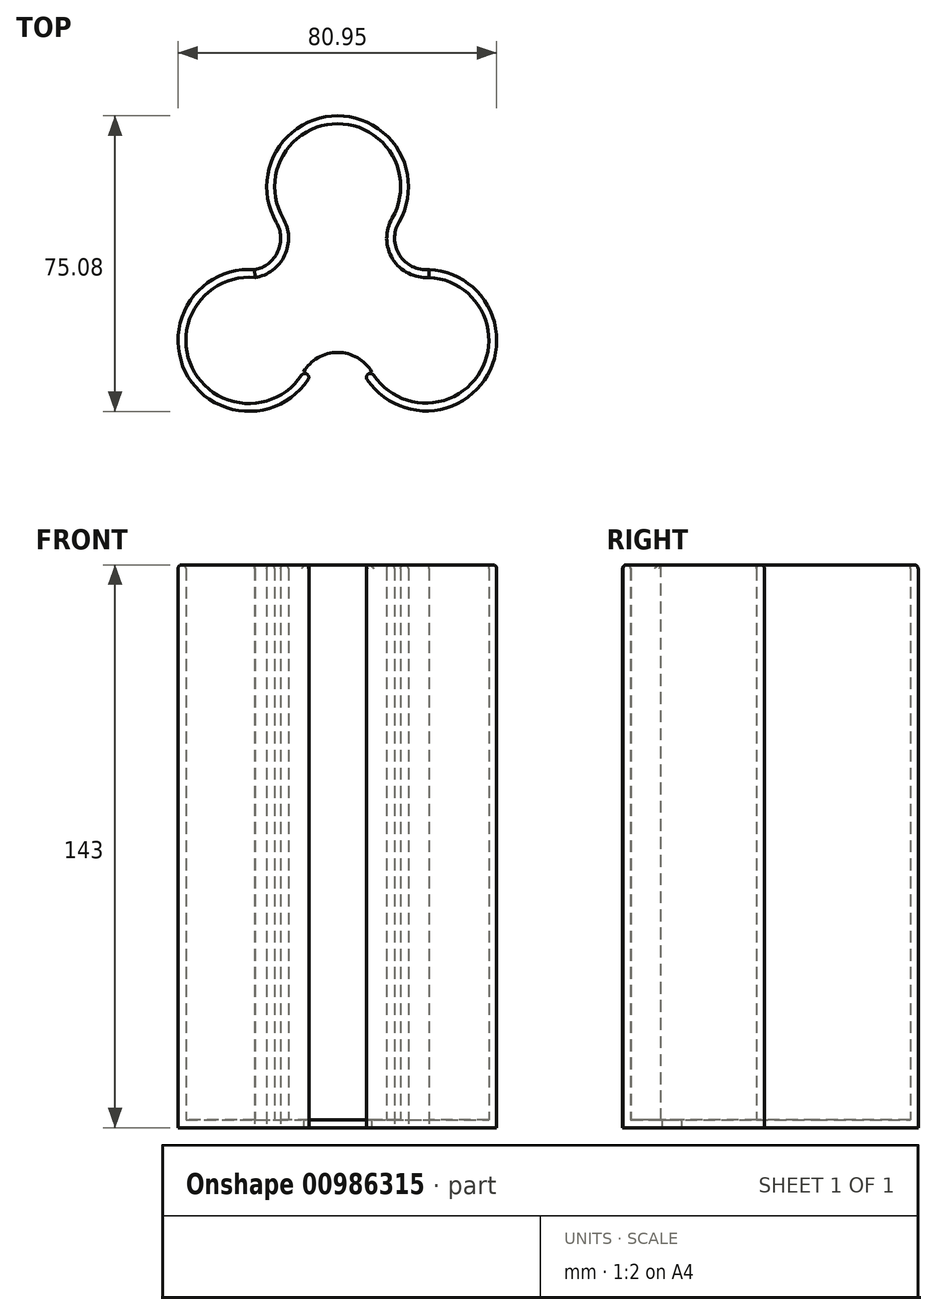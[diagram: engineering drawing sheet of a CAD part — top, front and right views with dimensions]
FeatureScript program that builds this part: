
annotation { "Feature Type Name" : "Feature", "Feature Type Description" : "" }
export const myFeature = defineFeature(function(context is Context, id is Id, definition is map)
    precondition{}
    {
        {
            var Q0;
            Q0=qCreatedBy(makeId("Top.planeOp"),FACE);
            var sketch = newSketch(context, id + "F0", { "sketchPlane" : qUnion([Q0])});
            skArc(sketch, "E0", {"start": v(13, 18.5) * mm, "mid": v(0, 41) * mm, "end": v(-13, 18.5) * mm});
            skArc(sketch, "E1.1.0", {"start": v(-24.16, 1.87) * mm, "mid": v(-35.1, -21.26) * mm, "end": v(-9.53, -20.6) * mm});
            skArc(sketch, "E1.2.0", {"start": v(15.06, 0.04) * mm, "mid": v(15.05, 0.04) * mm, "end": v(15.04, 0.03) * mm});
            skPoint(sketch, "E1.center", {"position": v(0, 0) * mm});
            skArc(sketch, "E2", {"start": v(7.54, 13.02) * mm, "mid": v(7.53, 13.02) * mm, "end": v(7.52, 13.02) * mm});
            skLineSegment(sketch, "E3", {"start": v(7.57, -13) * mm, "end": v(7.45, -13) * mm, "construction": true});
            skArc(sketch, "E4", {"start": v(-24.16, 1.87) * mm, "mid": v(-13.37, 6.69) * mm, "end": v(-13, 18.5) * mm});
            skArc(sketch, "E5.1.0", {"start": v(9.53, -20.6) * mm, "mid": v(0, -15.1) * mm, "end": v(-9.53, -20.6) * mm});
            skArc(sketch, "E5.2.0", {"start": v(13, 18.5) * mm, "mid": v(13.14, 7.13) * mm, "end": v(23.27, 1.96) * mm});
            skLineSegment(sketch, "E6.trimOffspring", {"start": v(7.54, 13.02) * mm, "end": v(7.55, 13.04) * mm, "construction": true});
            skArc(sketch, "E7.trimOffspring", {"start": v(-7.52, 13.02) * mm, "mid": v(-7.53, 13.02) * mm, "end": v(-7.54, 13.02) * mm});
            skArc(sketch, "E8.trimOffspring", {"start": v(7.52, 13.02) * mm, "mid": v(7.54, 13.03) * mm, "end": v(7.55, 13.04) * mm});
            skArc(sketch, "E9.trimOffspring", {"start": v(-7.55, 13.04) * mm, "mid": v(-7.54, 13.03) * mm, "end": v(-7.52, 13.02) * mm});
            skArc(sketch, "E10.trimOffspring", {"start": v(-15.04, 0.02) * mm, "mid": v(-15.04, 0) * mm, "end": v(-15.04, -0.03) * mm});
            skLineSegment(sketch, "E11.trimOffspring", {"start": v(-7.54, 13.02) * mm, "end": v(-7.55, 13.04) * mm, "construction": true});
            skLineSegment(sketch, "E12.trimOffspring", {"start": v(-15.1, 0) * mm, "end": v(-15.04, 0.02) * mm, "construction": true});
            skArc(sketch, "E13.trimOffspring", {"start": v(-15.04, -0.03) * mm, "mid": v(-15.07, -0.01) * mm, "end": v(-15.1, 0) * mm});
            skLineSegment(sketch, "E14.trimOffspring", {"start": v(15.06, 0.04) * mm, "end": v(15.04, 0.02) * mm, "construction": true});
            skArc(sketch, "E15.trimOffspring", {"start": v(9.53, -20.6) * mm, "mid": v(35.22, -20.8) * mm, "end": v(23.27, 1.96) * mm});
            skLineSegment(sketch, "E16.trimOffspring", {"start": v(-7.5, -13) * mm, "end": v(-7.57, -13) * mm, "construction": true});
            skArc(sketch, "E17.0", {"start": v(-21, 2.9) * mm, "mid": v(-13.45, 8.56) * mm, "end": v(-13.86, 18) * mm});
            skArc(sketch, "E17.1", {"start": v(8.66, -21.1) * mm, "mid": v(0, -16.1) * mm, "end": v(-8.66, -21.1) * mm});
            skArc(sketch, "E17.2", {"start": v(8.66, -21.1) * mm, "mid": v(36.1, -21.28) * mm, "end": v(23.26, 2.96) * mm});
            skArc(sketch, "E17.3", {"start": v(-21, 2.9) * mm, "mid": v(-36.77, -20.38) * mm, "end": v(-8.66, -21.1) * mm});
            skArc(sketch, "E17.4", {"start": v(13.86, 18) * mm, "mid": v(14, 7.63) * mm, "end": v(23.26, 2.96) * mm});
            skArc(sketch, "E17.5", {"start": v(13.86, 18) * mm, "mid": v(0, 42) * mm, "end": v(-13.86, 18) * mm});
            skArc(sketch, "E18.0", {"start": v(-21.08, 4.9) * mm, "mid": v(-38.48, -21.42) * mm, "end": v(-6.93, -22.1) * mm});
            skArc(sketch, "E18.1", {"start": v(6.94, -22.12) * mm, "mid": v(37.84, -22.26) * mm, "end": v(23.22, 4.96) * mm});
            skArc(sketch, "E18.2", {"start": v(15.58, 17) * mm, "mid": v(15.73, 8.64) * mm, "end": v(23.22, 4.96) * mm});
            skArc(sketch, "E18.3", {"start": v(15.58, 17) * mm, "mid": v(0, 44) * mm, "end": v(-15.59, 17) * mm});
            skArc(sketch, "E18.4", {"start": v(-21.08, 4.9) * mm, "mid": v(-15.2, 9.53) * mm, "end": v(-15.59, 17) * mm});
            skLineSegment(sketch, "E19", {"start": v(-8.66, -21.1) * mm, "end": v(-6.93, -22.1) * mm});
            skLineSegment(sketch, "E20", {"start": v(6.94, -22.12) * mm, "end": v(8.66, -21.1) * mm});
            skSolve(sketch);
        }
        {
            var Q0;
            Q0=makeQuery(id+"F0.imprint","IMPRINT",FACE,{"disambiguationData":[TD([[makeQuery(id+"F0.imprint","IMPRINT",EDGE,{"derivedFrom":sQuery(id+"F0.wireOp",EDGE,"E0")}),-1.0]])]});
            var Q1;
            Q1=makeQuery(id+"F0.imprint","IMPRINT",FACE,{"disambiguationData":[TD([[makeQuery(id+"F0.imprint","IMPRINT",EDGE,{"derivedFrom":sQuery(id+"F0.wireOp",EDGE,"E0")}),1.0]])]});
            extrude(context, id + "F1", {"entities" : qUnion([Q0, Q1]), "depth" : 2 * mm, "offsetDistance" : 25 * mm});
        }
        {
            var Q0;
            Q0=makeQuery(id+"F0.imprint","IMPRINT",FACE,{"disambiguationData":[TD([[makeQuery(id+"F0.imprint","IMPRINT",EDGE,{"derivedFrom":sQuery(id+"F0.wireOp",EDGE,"E17.0")}),1.0]])]});
            extrude(context, id + "F2", {"entities" : qUnion([Q0]), "operationType" : NewBodyOperationType.ADD, "depth" : 143 * mm, "offsetDistance" : 25 * mm});
        }
        {
            var Q0;
            Q0=makeQuery(id+"F2.opExtrude","SWEPT_EDGE",EDGE,{"disambiguationData":[OSD([sQuery(id+"F0.wireOp",EDGE,"E18.0"),sQuery(id+"F0.wireOp",EDGE,"E19")])]});
            var Q1;
            Q1=makeQuery(id+"F2.boolean.opBoolean","SPLIT",EDGE,{"derivedFrom":makeQuery(id+"F2.opExtrude","SWEPT_EDGE",EDGE,{"disambiguationData":[OSD([sQuery(id+"F0.wireOp",EDGE,"E17.1"),sQuery(id+"F0.wireOp",EDGE,"E17.3"),sQuery(id+"F0.wireOp",EDGE,"E19")])]})});
            var Q2;
            Q2=makeQuery(id+"F2.opExtrude","CAP_EDGE",EDGE,{"disambiguationData":[OSD([sQuery(id+"F0.wireOp",EDGE,"E18.0")])],"isStart":false});
            var Q3;
            Q3=makeQuery(id+"F2.opExtrude","CAP_EDGE",EDGE,{"disambiguationData":[OSD([sQuery(id+"F0.wireOp",EDGE,"E17.3")])],"isStart":false});
            var Q4;
            Q4=makeQuery(id+"F2.opExtrude","CAP_EDGE",EDGE,{"disambiguationData":[OSD([sQuery(id+"F0.wireOp",EDGE,"E17.0")])],"isStart":false});
            var Q5;
            Q5=makeQuery(id+"F2.opExtrude","CAP_EDGE",EDGE,{"disambiguationData":[OSD([sQuery(id+"F0.wireOp",EDGE,"E18.4")])],"isStart":false});
            var Q6;
            Q6=makeQuery(id+"F2.opExtrude","CAP_EDGE",EDGE,{"disambiguationData":[OSD([sQuery(id+"F0.wireOp",EDGE,"E18.3")])],"isStart":false});
            var Q7;
            Q7=makeQuery(id+"F2.opExtrude","CAP_EDGE",EDGE,{"disambiguationData":[OSD([sQuery(id+"F0.wireOp",EDGE,"E17.5")])],"isStart":false});
            var Q8;
            Q8=makeQuery(id+"F2.opExtrude","CAP_EDGE",EDGE,{"disambiguationData":[OSD([sQuery(id+"F0.wireOp",EDGE,"E17.4")])],"isStart":false});
            var Q9;
            Q9=makeQuery(id+"F2.opExtrude","CAP_EDGE",EDGE,{"disambiguationData":[OSD([sQuery(id+"F0.wireOp",EDGE,"E18.2")])],"isStart":false});
            var Q10;
            Q10=makeQuery(id+"F2.opExtrude","CAP_EDGE",EDGE,{"disambiguationData":[OSD([sQuery(id+"F0.wireOp",EDGE,"E18.1")])],"isStart":false});
            var Q11;
            Q11=makeQuery(id+"F2.opExtrude","CAP_EDGE",EDGE,{"disambiguationData":[OSD([sQuery(id+"F0.wireOp",EDGE,"E17.2")])],"isStart":false});
            var Q12;
            Q12=makeQuery(id+"F2.boolean.opBoolean","SPLIT",EDGE,{"derivedFrom":makeQuery(id+"F2.opExtrude","SWEPT_EDGE",EDGE,{"disambiguationData":[OSD([sQuery(id+"F0.wireOp",EDGE,"E17.1"),sQuery(id+"F0.wireOp",EDGE,"E17.2"),sQuery(id+"F0.wireOp",EDGE,"E20")])]})});
            var Q13;
            Q13=makeQuery(id+"F2.opExtrude","SWEPT_EDGE",EDGE,{"disambiguationData":[OSD([sQuery(id+"F0.wireOp",EDGE,"E18.1"),sQuery(id+"F0.wireOp",EDGE,"E20")])]});
            fillet(context, id + "F3", {"entities" : qUnion([Q0, Q1, Q2, Q3, Q4, Q5, Q6, Q7, Q8, Q9, Q10, Q11, Q12, Q13]), "radius" : 0.98 * mm, "tangentPropagation" : true, "allowEdgeOverflow" : false});
        }
    });
